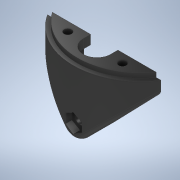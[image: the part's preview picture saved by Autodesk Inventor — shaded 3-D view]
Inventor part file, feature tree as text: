
AUTODESK INVENTOR PART (.ipt)
format: ipt  version: 2020 (Build 240168000, 168)  size: 352,768 bytes
history: native  units: in
note: dims shown in document units (in); Inventor stores cm internally (conversion verified against a paired STEP export)
features: sketch x8, extrude x3, revolve x2, fillet x2, hole x1
ambient origin geometry x8: Origin, YZ Plane, XZ Plane, XY Plane, X Axis, Y Axis, Z Axis, Center Point
bodies: Solid1 (feature_tree)
feature tree (16):
  sketch  "Sketch1"  dims[d2=1.74in d3=0.126in]
  revolve  "Revolution1"  [1 undecoded]
  extrude  "Extrusion1"  Depth=0.25in
  fillet  "Fillet1"  [1 undecoded]
  fillet  "Fillet2"  Radius=1.0in
  revolve  "Revolution2"  [1 undecoded]
  extrude  "Extrusion8"  Depth=1.5in
  extrude  "Extrusion9"  Depth=0.75in
  hole  "Hole5"  [1 undecoded]
  sketch  "Sketch2"  dims[d5=0.25in d7=0.25in d9=180.0deg d10=1.0in]
  sketch  "Sketch9"  dims[d11=1.85in d12=0.0in d16=1.382in d17=0.0in]
  sketch  "Sketch10"  dims[d46=1.25in d47=1.5in]
  sketch  "Sketch12"  dims[d48=0.205in d49=0.75in d50=0.3438in d51=1.0in d52=0.5635in d53=1.0in d54=0.8108in]
  sketch  "Sketch13"  dims[d55=0.266in d56=0.75in d57=0.875in d58=0.3125in d59=0.5635in d60=1.0in d61=0.8108in d65=0.0312in]
  sketch  "Sketch14"  dims[d66=0.125in d67=1.375in]
  sketch  "Sketch15"  dims[d78=90.0deg d91=0.4475in d92=0.1875in d93=0.0in d94=0.2in d95=0.0in d98=0.51in d102=0.5625in d105=0.4359in d106=0.2184in d107=0.375in d108=0.5in d109=0.375in d110=0.25in d111=1.2in d112=0.35in d113=0.75in d114=0.51in d115=0.188in d116=0.5635in d117=0.25in d118=0.0in d119=1.85in]
note: 4 required parameter values undecoded (feature->parameter linkage not recoverable at this tier; creation-order binding heuristic only, values carry confidence <= 0.55)